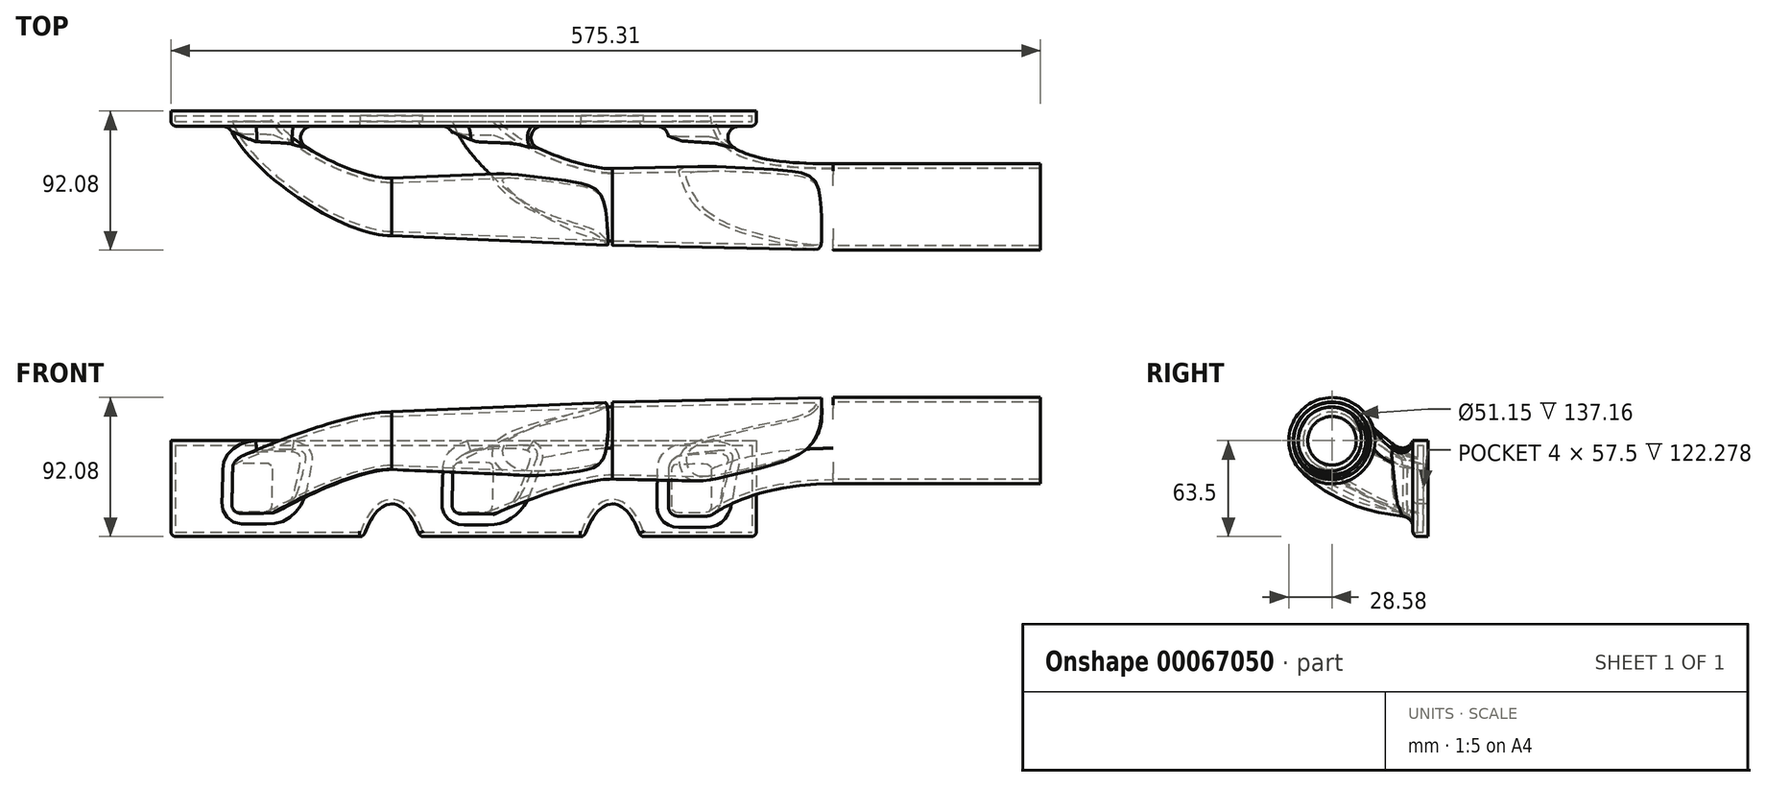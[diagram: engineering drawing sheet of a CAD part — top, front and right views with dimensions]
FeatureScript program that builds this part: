
annotation { "Feature Type Name" : "Feature", "Feature Type Description" : "" }
export const myFeature = defineFeature(function(context is Context, id is Id, definition is map)
    precondition{}
    {
        {
            var Q0;
            Q0=qCreatedBy(makeId("Front.planeOp"),FACE);
            var sketch = newSketch(context, id + "F0", { "sketchPlane" : qUnion([Q0])});
            skLineSegment(sketch, "E0.bottom", {"start": v(-146.05, 0) * mm, "end": v(241.3, 0) * mm});
            skLineSegment(sketch, "E0.top", {"start": v(-146.05, -63.5) * mm, "end": v(-18.63, -63.5) * mm});
            skLineSegment(sketch, "E0.left", {"start": v(-146.05, 0) * mm, "end": v(-146.05, -63.5) * mm});
            skLineSegment(sketch, "E0.right", {"start": v(241.3, 0) * mm, "end": v(241.3, -63.5) * mm});
            skEllipticalArc(sketch, "E1", {});
            skEllipticalArc(sketch, "E2.1.0.0", {});
            skLineSegment(sketch, "E3.trimOffspring", {"start": v(18.63, -63.5) * mm, "end": v(127.42, -63.5) * mm});
            skLineSegment(sketch, "E4.trimOffspring", {"start": v(164.68, -63.5) * mm, "end": v(241.3, -63.5) * mm});
            const initialGuessF0  = {"E1": [0, -0.09918, 0, 1, 0.05734, 0.023805, 5.3840067622967815, 0.8991785448828046], "E2.1.0.0": [0.14605, -0.09918, 0, 1, 0.05734, 0.023805, 5.3840067622967815, 0.8991785448828046]};
            skSetInitialGuess(sketch, initialGuessF0);
            skSolve(sketch);
        }
        {
            var Q0;
            Q0=qCreatedBy(makeId("Right.planeOp"),FACE);
            cPlane(context, id + "F1", {"entities" : qUnion([Q0]), "cplaneType" : CPlaneType.OFFSET, "offset" : 146.05 * mm, "width" : 152.4 * mm, "height" : 152.4 * mm});
        }
        {
            var Q0;
            Q0=qCreatedBy(id+"F1.planeOp",FACE);
            cPlane(context, id + "F2", {"entities" : qUnion([Q0]), "cplaneType" : CPlaneType.OFFSET, "offset" : 146.05 * mm, "width" : 152.4 * mm, "height" : 152.4 * mm});
        }
        {
            var Q0;
            Q0=qCreatedBy(makeId("Front.planeOp"),FACE);
            var sketch = newSketch(context, id + "F3", { "sketchPlane" : qUnion([Q0])});
            skLineSegment(sketch, "E5.rect.bottom", {"start": v(-103.5, -12.7) * mm, "end": v(-84.45, -12.7) * mm});
            skArc(sketch, "E6.filletArc", {"start": v(-78.1, -19.05) * mm, "mid": v(-79.96, -14.56) * mm, "end": v(-84.45, -12.7) * mm});
            skLineSegment(sketch, "E5.rect.right", {"start": v(-78.1, -19.05) * mm, "end": v(-78.1, -44.45) * mm});
            skArc(sketch, "E7.filletArc", {"start": v(-84.45, -50.8) * mm, "mid": v(-79.96, -48.94) * mm, "end": v(-78.1, -44.45) * mm});
            skLineSegment(sketch, "E5.rect.top", {"start": v(-103.5, -50.8) * mm, "end": v(-84.45, -50.8) * mm});
            skArc(sketch, "E8.filletArc", {"start": v(-109.86, -44.45) * mm, "mid": v(-108, -48.94) * mm, "end": v(-103.5, -50.8) * mm});
            skLineSegment(sketch, "E5.rect.left", {"start": v(-109.86, -19.05) * mm, "end": v(-109.86, -44.45) * mm});
            skArc(sketch, "E9.filletArc", {"start": v(-103.5, -12.7) * mm, "mid": v(-108, -14.56) * mm, "end": v(-109.86, -19.05) * mm});
            skLineSegment(sketch, "E10", {"start": v(-137.86, -31.75) * mm, "end": v(-109.86, -31.75) * mm, "construction": true});
            skPoint(sketch, "E10.startSnap0", {"position": v(-109.86, -31.75) * mm});
            skSolve(sketch);
        }
        {
            var Q0;
            Q0=qCreatedBy(makeId("Front.planeOp"),FACE);
            var sketch = newSketch(context, id + "F4", { "sketchPlane" : qUnion([Q0])});
            skLineSegment(sketch, "E11.rect.bottom", {"start": v(42.55, -12.7) * mm, "end": v(61.6, -12.7) * mm});
            skArc(sketch, "E12.filletArc", {"start": v(67.95, -19.05) * mm, "mid": v(66.09, -14.56) * mm, "end": v(61.6, -12.7) * mm});
            skLineSegment(sketch, "E11.rect.right", {"start": v(67.95, -19.05) * mm, "end": v(67.95, -44.45) * mm});
            skArc(sketch, "E13.filletArc", {"start": v(61.6, -50.8) * mm, "mid": v(66.09, -48.94) * mm, "end": v(67.95, -44.45) * mm});
            skLineSegment(sketch, "E11.rect.top", {"start": v(42.55, -50.8) * mm, "end": v(61.6, -50.8) * mm});
            skArc(sketch, "E14.filletArc", {"start": v(36.2, -44.45) * mm, "mid": v(38.05, -48.94) * mm, "end": v(42.55, -50.8) * mm});
            skLineSegment(sketch, "E11.rect.left", {"start": v(36.2, -19.05) * mm, "end": v(36.2, -44.45) * mm});
            skArc(sketch, "E15.filletArc", {"start": v(42.55, -12.7) * mm, "mid": v(38.05, -14.56) * mm, "end": v(36.2, -19.05) * mm});
            skLineSegment(sketch, "E16", {"start": v(36.2, -31.75) * mm, "end": v(-146.05, -31.75) * mm, "construction": true});
            skSolve(sketch);
        }
        {
            var Q0;
            Q0=qCreatedBy(makeId("Front.planeOp"),FACE);
            var sketch = newSketch(context, id + "F5", { "sketchPlane" : qUnion([Q0])});
            skLineSegment(sketch, "E17.rect.bottom", {"start": v(188.6, -12.7) * mm, "end": v(207.65, -12.7) * mm});
            skArc(sketch, "E18.filletArc", {"start": v(214, -19.05) * mm, "mid": v(212.14, -14.56) * mm, "end": v(207.65, -12.7) * mm});
            skLineSegment(sketch, "E17.rect.right", {"start": v(214, -19.05) * mm, "end": v(214, -44.45) * mm});
            skArc(sketch, "E19.filletArc", {"start": v(207.65, -50.8) * mm, "mid": v(212.14, -48.94) * mm, "end": v(214, -44.45) * mm});
            skLineSegment(sketch, "E17.rect.top", {"start": v(188.6, -50.8) * mm, "end": v(207.65, -50.8) * mm});
            skArc(sketch, "E20.filletArc", {"start": v(182.25, -44.45) * mm, "mid": v(184.1, -48.94) * mm, "end": v(188.6, -50.8) * mm});
            skLineSegment(sketch, "E17.rect.left", {"start": v(182.25, -19.05) * mm, "end": v(182.25, -44.45) * mm});
            skArc(sketch, "E21.filletArc", {"start": v(188.6, -12.7) * mm, "mid": v(184.1, -14.56) * mm, "end": v(182.25, -19.05) * mm});
            skLineSegment(sketch, "E22", {"start": v(182.25, -31.75) * mm, "end": v(-146.05, -31.75) * mm, "construction": true});
            skSolve(sketch);
        }
        {
            var Q0;
            Q0=qCreatedBy(makeId("Right.planeOp"),FACE);
            cPlane(context, id + "F6", {"entities" : qUnion([Q0]), "cplaneType" : CPlaneType.OFFSET, "offset" : 146.05 * mm, "width" : 152.4 * mm, "height" : 152.4 * mm});
        }
        {
            var Q0;
            Q0=qCreatedBy(makeId("Right.planeOp"),FACE);
            var sketch = newSketch(context, id + "F7", { "sketchPlane" : qUnion([Q0])});
            skCircle(sketch, "E23", {"center": v(-63.5, 0) * mm, "radius": 19.05 * mm});
            skSolve(sketch);
        }
        {
            var Q0;
            Q0=qCreatedBy(id+"F6.planeOp",FACE);
            var sketch = newSketch(context, id + "F8", { "sketchPlane" : qUnion([Q0])});
            skCircle(sketch, "E24", {"center": v(-63.5, 0) * mm, "radius": 25.4 * mm});
            skSolve(sketch);
        }
        {
            var Q0;
            Q0=qCreatedBy(id+"F2.planeOp",FACE);
            var sketch = newSketch(context, id + "F9", { "sketchPlane" : qUnion([Q0])});
            skCircle(sketch, "E25", {"center": v(-63.5, 0) * mm, "radius": 28.57 * mm});
            skSolve(sketch);
        }
        {
            var Q0;
            Q0=makeQuery(id+"F7.imprint","IMPRINT",FACE,{"disambiguationData":[TD([[makeQuery(id+"F7.imprint","IMPRINT",EDGE,{"derivedFrom":sQuery(id+"F7.wireOp",EDGE,"E23")}),1.0]])]});
            var Q1;
            Q1=makeQuery(id+"F8.imprint","IMPRINT",FACE,{"disambiguationData":[TD([[makeQuery(id+"F8.imprint","IMPRINT",EDGE,{"derivedFrom":sQuery(id+"F8.wireOp",EDGE,"E24")}),1.0]])]});
            loft(context, id + "F10", {"sheetProfilesArray" : [{ "sheetProfileEntities" : qUnion([Q0]) }, { "sheetProfileEntities" : qUnion([Q1]) }]});
        }
        {
            var Q1;
            Q1=qSketchRegion(id+"F8",true);
            var Q2;
            Q2=qSketchRegion(id+"F9",true);
            loft(context, id + "F11", {"operationType" : NewBodyOperationType.ADD, "sheetProfilesArray" : [{ "sheetProfileEntities" : qUnion([Q1]) }, { "sheetProfileEntities" : qUnion([Q2]) }]});
        }
        {
            var Q1;
            Q1=qSketchRegion(id+"F7",true);
            var Q2;
            Q2=qSketchRegion(id+"F3",true);
            loft(context, id + "F12", {"operationType" : NewBodyOperationType.ADD, "startCondition" : LoftEndDerivativeType.NORMAL_TO_PROFILE, "startMagnitude" : 1, "endCondition" : LoftEndDerivativeType.NORMAL_TO_PROFILE, "endMagnitude" : 1, "sheetProfilesArray" : [{ "sheetProfileEntities" : qUnion([Q1]) }, { "sheetProfileEntities" : qUnion([Q2]) }]});
        }
        {
            var Q1;
            Q1=qSketchRegion(id+"F9",true);
            var Q2;
            Q2=qSketchRegion(id+"F5",true);
            loft(context, id + "F13", {"operationType" : NewBodyOperationType.ADD, "startCondition" : LoftEndDerivativeType.NORMAL_TO_PROFILE, "startMagnitude" : 2, "endCondition" : LoftEndDerivativeType.NORMAL_TO_PROFILE, "endMagnitude" : 2, "sheetProfilesArray" : [{ "sheetProfileEntities" : qUnion([Q1]) }, { "sheetProfileEntities" : qUnion([Q2]) }]});
        }
        {
            var Q0;
            Q0=makeQuery(id+"F9.imprint","IMPRINT",FACE,{"disambiguationData":[TD([[makeQuery(id+"F9.imprint","IMPRINT",EDGE,{"derivedFrom":sQuery(id+"F9.wireOp",EDGE,"E25")}),1.0]])]});
            var sketch = newSketch(context, id + "F14", { "sketchPlane" : qUnion([Q0])});
            skCircle(sketch, "E26", {"center": v(-63.5, 0) * mm, "radius": 28.57 * mm});
            skSolve(sketch);
        }
        {
            var Q0;
            Q0=qSketchRegion(id+"F14",true);
            extrude(context, id + "F15", {"entities" : qUnion([Q0]), "operationType" : NewBodyOperationType.ADD, "depth" : 137.16 * mm});
        }
        {
            var Q0;
            Q0=qSketchRegion(id+"F0",true);
            extrude(context, id + "F16", {"entities" : qUnion([Q0]), "operationType" : NewBodyOperationType.ADD, "depth" : 10 * mm});
        }
        {
            var Q1;
            Q1=qSketchRegion(id+"F8",true);
            var Q2;
            Q2=qSketchRegion(id+"F4",true);
            loft(context, id + "F17", {"operationType" : NewBodyOperationType.ADD, "startCondition" : LoftEndDerivativeType.NORMAL_TO_PROFILE, "startMagnitude" : 1, "endCondition" : LoftEndDerivativeType.NORMAL_TO_PROFILE, "endMagnitude" : 1, "sheetProfilesArray" : [{ "sheetProfileEntities" : qUnion([Q1]) }, { "sheetProfileEntities" : qUnion([Q2]) }]});
        }
        {
            var Q0;
            Q0=makeQuery(id+"F15.opExtrude","CAP_FACE",FACE,{"disambiguationData":[OSD([sQuery(id+"F14.wireOp",EDGE,"E26")])],"isStart":false});
            var Q1;
            Q1=makeQuery(id+"F15.opExtrude","CAP_FACE",FACE,{"disambiguationData":[OSD([sQuery(id+"F14.wireOp",EDGE,"E26")])],"isStart":false});
            shell(context, id + "F18", {"entities" : qUnion([Q0, Q1]), "thickness" : 3 * mm});
        }
        {
            var Q0;
            Q0=makeQuery(id+"F16.boolean.opBoolean","INTERSECT",EDGE,{"derivedFrom":[makeQuery(id+"F12.opLoft","SWEPT_FACE",FACE,{"disambiguationData":[OSD([sQuery(id+"F3.wireOp",EDGE,"E5.rect.bottom"),sQuery(id+"F3.wireOp",EDGE,"E6.filletArc"),sQuery(id+"F3.wireOp",EDGE,"E5.rect.right"),sQuery(id+"F3.wireOp",EDGE,"E7.filletArc"),sQuery(id+"F3.wireOp",EDGE,"E9.filletArc"),sQuery(id+"F7.wireOp",EDGE,"E23")])]}),makeQuery(id+"F16.opExtrude","CAP_FACE",FACE,{"disambiguationData":[OSD([sQuery(id+"F0.wireOp",EDGE,"E0.bottom"),sQuery(id+"F0.wireOp",EDGE,"E0.top"),sQuery(id+"F0.wireOp",EDGE,"E0.left"),sQuery(id+"F0.wireOp",EDGE,"E0.right"),sQuery(id+"F0.wireOp",EDGE,"E1"),sQuery(id+"F0.wireOp",EDGE,"E2.1.0.0"),sQuery(id+"F0.wireOp",EDGE,"E3.trimOffspring"),sQuery(id+"F0.wireOp",EDGE,"E4.trimOffspring")])],"isStart":false})]});
            fillet(context, id + "F19", {"entities" : qUnion([Q0]), "radius" : 7.5 * mm, "tangentPropagation" : true, "allowEdgeOverflow" : false});
        }
        {
            var Q0;
            Q0=makeQuery(id+"F17.boolean.opBoolean","INTERSECT",EDGE,{"derivedFrom":[makeQuery(id+"F16.opExtrude","CAP_FACE",FACE,{"disambiguationData":[OSD([sQuery(id+"F0.wireOp",EDGE,"E0.bottom"),sQuery(id+"F0.wireOp",EDGE,"E0.top"),sQuery(id+"F0.wireOp",EDGE,"E0.left"),sQuery(id+"F0.wireOp",EDGE,"E0.right"),sQuery(id+"F0.wireOp",EDGE,"E1"),sQuery(id+"F0.wireOp",EDGE,"E2.1.0.0"),sQuery(id+"F0.wireOp",EDGE,"E3.trimOffspring"),sQuery(id+"F0.wireOp",EDGE,"E4.trimOffspring")])],"isStart":false}),makeQuery(id+"F17.opLoft","SWEPT_FACE",FACE,{"disambiguationData":[OSD([sQuery(id+"F4.wireOp",EDGE,"E11.rect.bottom"),sQuery(id+"F4.wireOp",EDGE,"E12.filletArc"),sQuery(id+"F4.wireOp",EDGE,"E11.rect.right"),sQuery(id+"F4.wireOp",EDGE,"E13.filletArc"),sQuery(id+"F4.wireOp",EDGE,"E15.filletArc"),sQuery(id+"F8.wireOp",EDGE,"E24")])]})]});
            fillet(context, id + "F20", {"entities" : qUnion([Q0]), "radius" : 7.5 * mm, "tangentPropagation" : true, "allowEdgeOverflow" : false});
        }
        {
            var Q0;
            Q0=makeQuery(id+"F16.boolean.opBoolean","INTERSECT",EDGE,{"derivedFrom":[makeQuery(id+"F13.opLoft","SWEPT_FACE",FACE,{"disambiguationData":[OSD([sQuery(id+"F5.wireOp",EDGE,"E17.rect.bottom"),sQuery(id+"F5.wireOp",EDGE,"E18.filletArc"),sQuery(id+"F5.wireOp",EDGE,"E17.rect.right"),sQuery(id+"F5.wireOp",EDGE,"E19.filletArc"),sQuery(id+"F5.wireOp",EDGE,"E21.filletArc"),sQuery(id+"F9.wireOp",EDGE,"E25")])]}),makeQuery(id+"F16.opExtrude","CAP_FACE",FACE,{"disambiguationData":[OSD([sQuery(id+"F0.wireOp",EDGE,"E0.bottom"),sQuery(id+"F0.wireOp",EDGE,"E0.top"),sQuery(id+"F0.wireOp",EDGE,"E0.left"),sQuery(id+"F0.wireOp",EDGE,"E0.right"),sQuery(id+"F0.wireOp",EDGE,"E1"),sQuery(id+"F0.wireOp",EDGE,"E2.1.0.0"),sQuery(id+"F0.wireOp",EDGE,"E3.trimOffspring"),sQuery(id+"F0.wireOp",EDGE,"E4.trimOffspring")])],"isStart":false})]});
            fillet(context, id + "F21", {"entities" : qUnion([Q0]), "radius" : 7.5 * mm, "tangentPropagation" : true, "allowEdgeOverflow" : false});
        }
        {
            var Q0;
            Q0=makeQuery(id+"F16.opExtrude","CAP_EDGE",EDGE,{"disambiguationData":[OSD([sQuery(id+"F0.wireOp",EDGE,"E0.top")])],"isStart":false});
            fillet(context, id + "F22", {"entities" : qUnion([Q0]), "radius" : 3.5 * mm, "tangentPropagation" : true, "allowEdgeOverflow" : false});
        }
        {
            var Q0;
            Q0=makeQuery(id+"F16.opExtrude","CAP_EDGE",EDGE,{"disambiguationData":[OSD([sQuery(id+"F0.wireOp",EDGE,"E0.left")])],"isStart":false});
            fillet(context, id + "F23", {"entities" : qUnion([Q0]), "radius" : 3.5 * mm, "tangentPropagation" : true, "allowEdgeOverflow" : false});
        }
        {
            var Q0;
            Q0=makeQuery(id+"F16.opExtrude","CAP_EDGE",EDGE,{"disambiguationData":[OSD([sQuery(id+"F0.wireOp",EDGE,"E1")])],"isStart":false});
            fillet(context, id + "F24", {"entities" : qUnion([Q0]), "radius" : 3.5 * mm, "tangentPropagation" : true, "allowEdgeOverflow" : false});
        }
        {
            var Q0;
            Q0=makeQuery(id+"F16.opExtrude","CAP_EDGE",EDGE,{"disambiguationData":[OSD([sQuery(id+"F0.wireOp",EDGE,"E3.trimOffspring")])],"isStart":false});
            fillet(context, id + "F25", {"entities" : qUnion([Q0]), "radius" : 3.5 * mm, "tangentPropagation" : true, "allowEdgeOverflow" : false});
        }
        {
            var Q0;
            Q0=makeQuery(id+"F16.opExtrude","CAP_EDGE",EDGE,{"disambiguationData":[OSD([sQuery(id+"F0.wireOp",EDGE,"E2.1.0.0")])],"isStart":false});
            fillet(context, id + "F26", {"entities" : qUnion([Q0]), "radius" : 3.5 * mm, "tangentPropagation" : true, "allowEdgeOverflow" : false});
        }
        {
            var Q0;
            Q0=makeQuery(id+"F16.opExtrude","CAP_EDGE",EDGE,{"disambiguationData":[OSD([sQuery(id+"F0.wireOp",EDGE,"E4.trimOffspring")])],"isStart":false});
            fillet(context, id + "F27", {"entities" : qUnion([Q0]), "radius" : 3.5 * mm, "tangentPropagation" : true, "allowEdgeOverflow" : false});
        }
        {
            var Q0;
            Q0=makeQuery(id+"F16.opExtrude","CAP_EDGE",EDGE,{"disambiguationData":[OSD([sQuery(id+"F0.wireOp",EDGE,"E0.right")])],"isStart":false});
            fillet(context, id + "F28", {"entities" : qUnion([Q0]), "radius" : 3.5 * mm, "tangentPropagation" : true, "allowEdgeOverflow" : false});
        }
    });
